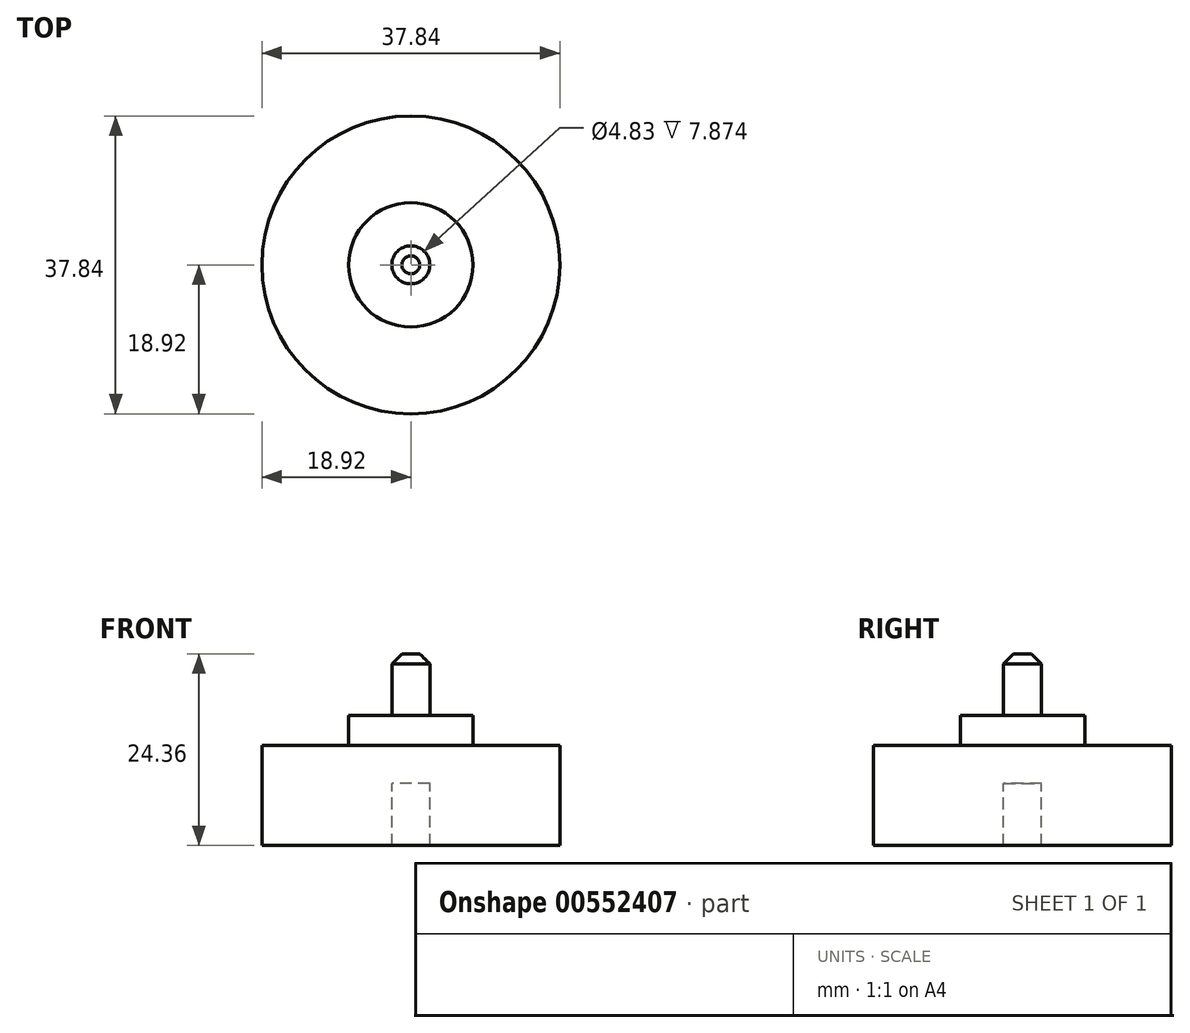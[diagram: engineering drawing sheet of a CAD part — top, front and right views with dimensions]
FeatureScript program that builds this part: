
annotation { "Feature Type Name" : "Feature", "Feature Type Description" : "" }
export const myFeature = defineFeature(function(context is Context, id is Id, definition is map)
    precondition{}
    {
        {
            var Q0;
            Q0=qCreatedBy(makeId("Front.planeOp"),FACE);
            var sketch = newSketch(context, id + "F0", { "sketchPlane" : qUnion([Q0])});
            skLineSegment(sketch, "E0", {"start": v(18.92, 0) * mm, "end": v(18.92, 12.7) * mm});
            skLineSegment(sketch, "E1", {"start": v(18.92, 12.7) * mm, "end": v(7.9, 12.7) * mm});
            skLineSegment(sketch, "E2", {"start": v(2.41, 16.51) * mm, "end": v(7.9, 16.51) * mm});
            skLineSegment(sketch, "E3", {"start": v(7.9, 16.51) * mm, "end": v(7.9, 12.7) * mm});
            skLineSegment(sketch, "E4", {"start": v(2.41, 0) * mm, "end": v(2.41, 7.87) * mm});
            skLineSegment(sketch, "E5", {"start": v(2.41, 7.87) * mm, "end": v(0, 7.87) * mm});
            skLineSegment(sketch, "E6", {"start": v(2.41, 0) * mm, "end": v(18.92, 0) * mm});
            skLineSegment(sketch, "E7", {"start": v(0, 24.36) * mm, "end": v(2.41, 24.36) * mm});
            skLineSegment(sketch, "E8", {"start": v(2.41, 24.36) * mm, "end": v(2.41, 16.51) * mm});
            skPoint(sketch, "E9.start.orphan", {"position": v(0, 12.7) * mm});
            skPoint(sketch, "E10.start.orphan", {"position": v(0, 16.51) * mm});
            skLineSegment(sketch, "E11", {"start": v(0, 24.36) * mm, "end": v(0, 7.87) * mm});
            skSolve(sketch);
        }
        {
            var Q0;
            Q0 = qSketchRegion(id + "F0", true);
            var Q1;
            Q1=sQuery(id+"F0.wireOp",EDGE,"E11");
            revolve(context, id + "F1", {"entities" : qUnion([Q0]), "axis" : qUnion([Q1]), "revolveType" : RevolveType.FULL});
        }
        {
            var Q0;
            Q0=makeQuery(id+"F1.opRevolve","SWEPT_EDGE",EDGE,{"disambiguationData":[OSD([sQuery(id+"F0.wireOp",EDGE,"E7"),sQuery(id+"F0.wireOp",EDGE,"E8")])]});
            chamfer(context, id + "F2", {"entities" : qUnion([Q0]), "width" : 1.27 * mm, "tangentPropagation" : true});
        }
    });
